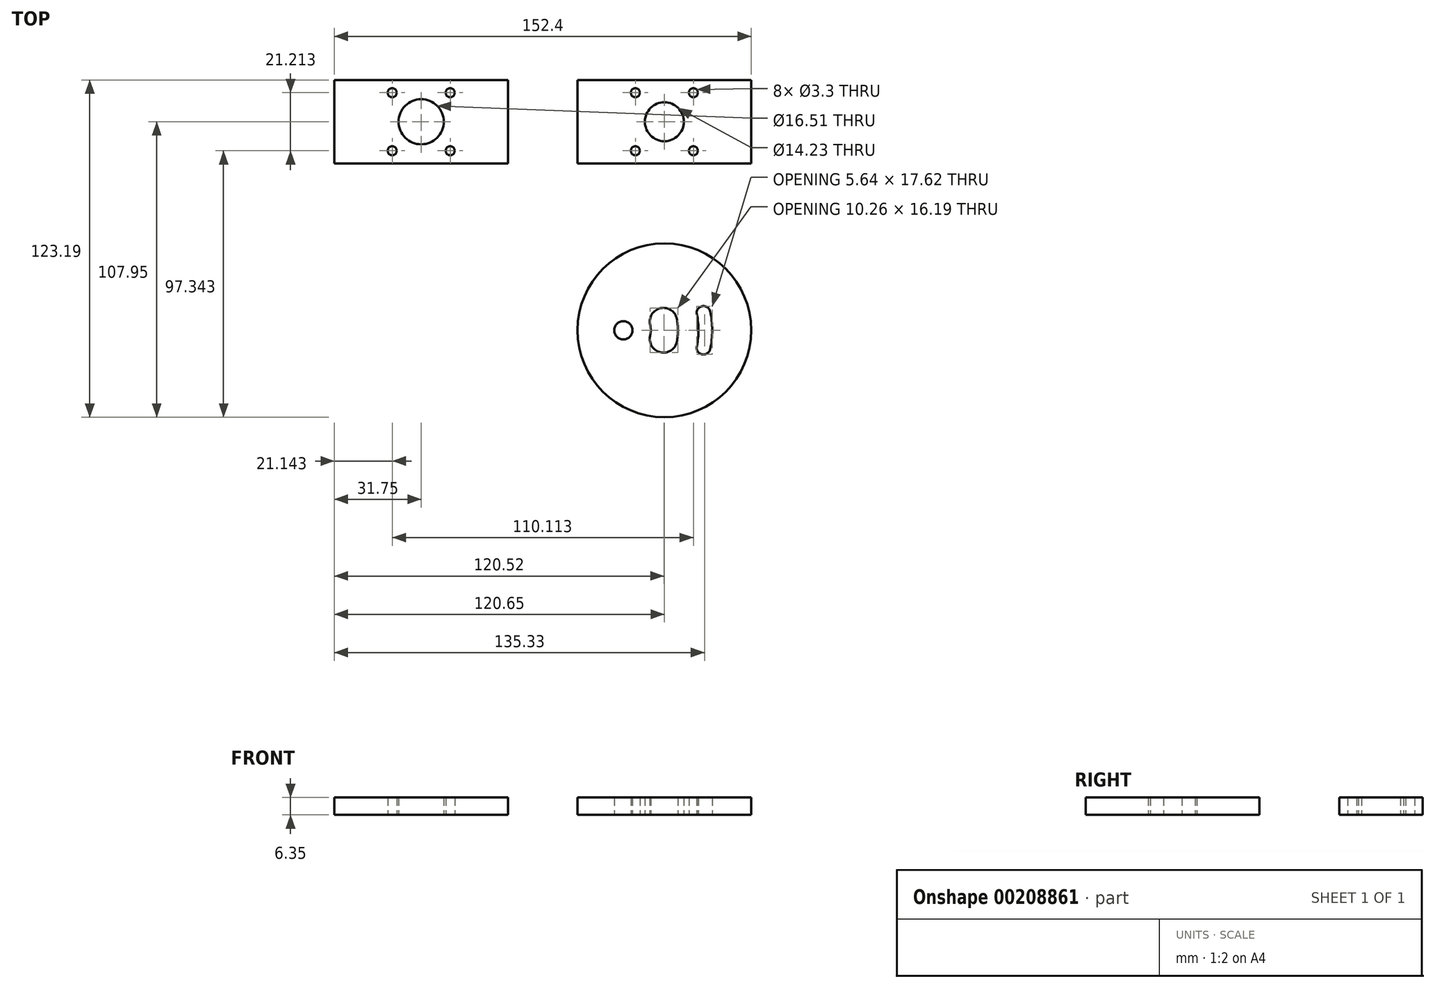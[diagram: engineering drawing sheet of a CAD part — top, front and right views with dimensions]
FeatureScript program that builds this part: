
annotation { "Feature Type Name" : "Feature", "Feature Type Description" : "" }
export const myFeature = defineFeature(function(context is Context, id is Id, definition is map)
    precondition{}
    {
        {
            var Q0;
            Q0=qCreatedBy(makeId("Top.planeOp"),FACE);
            var sketch = newSketch(context, id + "F0", { "sketchPlane" : qUnion([Q0])});
            skCircle(sketch, "E0", {"center": v(0, 0) * mm, "radius": 8.26 * mm});
            skCircle(sketch, "E1", {"center": v(88.9, 0) * mm, "radius": 7.12 * mm});
            skCircle(sketch, "E2", {"center": v(88.9, -76.2) * mm, "radius": 31.75 * mm});
            skCircle(sketch, "E3", {"center": v(73.9, -76.2) * mm, "radius": 3.35 * mm});
            skCircle(sketch, "E4", {"center": v(73.9, -76.2) * mm, "radius": 30 * mm, "construction": true});
            skArc(sketch, "E5", {"start": v(100.78, -82.02) * mm, "mid": v(101.4, -76.2) * mm, "end": v(100.78, -70.38) * mm});
            skArc(sketch, "E6", {"start": v(105.66, -83.08) * mm, "mid": v(106.4, -76.2) * mm, "end": v(105.66, -69.32) * mm});
            skCircle(sketch, "E7", {"center": v(88.9, -76.2) * mm, "radius": 15 * mm, "construction": true});
            skArc(sketch, "E8", {"start": v(103.4, -72.34) * mm, "mid": v(103.52, -72.33) * mm, "end": v(103.65, -72.31) * mm});
            skArc(sketch, "E9", {"start": v(100.78, -82.02) * mm, "mid": v(102.7, -85) * mm, "end": v(105.66, -83.08) * mm});
            skArc(sketch, "E10.trimOffspring", {"start": v(105.66, -69.32) * mm, "mid": v(102.7, -67.4) * mm, "end": v(100.78, -70.38) * mm});
            skArc(sketch, "E11.trimOffspring", {"start": v(103.65, -80.09) * mm, "mid": v(103.52, -80.07) * mm, "end": v(103.4, -80.06) * mm});
            skCircle(sketch, "E12", {"center": v(73.9, -76.2) * mm, "radius": 15 * mm, "construction": true});
            skArc(sketch, "E13", {"start": v(93.45, -71.97) * mm, "mid": v(87.5, -68.14) * mm, "end": v(83.67, -74.08) * mm});
            skArc(sketch, "E14", {"start": v(83.67, -78.32) * mm, "mid": v(87.5, -84.26) * mm, "end": v(93.45, -80.43) * mm});
            skArc(sketch, "E15.trimOffspring", {"start": v(83.67, -78.32) * mm, "mid": v(83.9, -76.2) * mm, "end": v(83.67, -74.08) * mm});
            skArc(sketch, "E16.trimOffspring", {"start": v(93.45, -80.43) * mm, "mid": v(93.9, -76.2) * mm, "end": v(93.45, -71.97) * mm});
            skLineSegment(sketch, "E17", {"start": v(-31.75, 15.24) * mm, "end": v(31.75, 15.24) * mm});
            skLineSegment(sketch, "E18.trimOffspring", {"start": v(57.15, 15.24) * mm, "end": v(120.65, 15.24) * mm});
            skLineSegment(sketch, "E19", {"start": v(0, 0) * mm, "end": v(88.9, 0) * mm, "construction": true});
            skLineSegment(sketch, "E20.0.MirrorCS", {"start": v(-31.75, -15.24) * mm, "end": v(31.75, -15.24) * mm});
            skLineSegment(sketch, "E21.0.MirrorCS", {"start": v(57.15, -15.24) * mm, "end": v(120.65, -15.24) * mm});
            skCircle(sketch, "E22", {"center": v(88.9, 0) * mm, "radius": 15 * mm, "construction": true});
            skLineSegment(sketch, "E23", {"start": v(88.9, 0) * mm, "end": v(88.9, 11.57) * mm, "construction": true});
            skLineSegment(sketch, "E24", {"start": v(88.9, 0) * mm, "end": v(76.23, 12.67) * mm, "construction": true});
            skCircle(sketch, "E25", {"center": v(78.3, 10.6) * mm, "radius": 1.65 * mm});
            skCircle(sketch, "E26.0.MirrorC", {"center": v(99.5, 10.6) * mm, "radius": 1.65 * mm});
            skCircle(sketch, "E27.0.MirrorC", {"center": v(78.3, -10.6) * mm, "radius": 1.65 * mm});
            skCircle(sketch, "E28.0.MirrorC", {"center": v(99.5, -10.6) * mm, "radius": 1.65 * mm});
            skLineSegment(sketch, "E29", {"start": v(31.75, -15.24) * mm, "end": v(31.75, 15.24) * mm});
            skLineSegment(sketch, "E30", {"start": v(-31.75, -15.24) * mm, "end": v(-31.75, 15.24) * mm});
            skLineSegment(sketch, "E31", {"start": v(57.15, 15.24) * mm, "end": v(57.15, -15.24) * mm});
            skLineSegment(sketch, "E32", {"start": v(120.65, -15.24) * mm, "end": v(120.65, 15.24) * mm});
            skPoint(sketch, "E33.center.orphan", {"position": v(15, 0) * mm});
            skPoint(sketch, "E34.center.orphan", {"position": v(0, -15) * mm});
            skPoint(sketch, "E35.center.orphan", {"position": v(-15, 0) * mm});
            skPoint(sketch, "E36.center.orphan", {"position": v(0, 15) * mm});
            skCircle(sketch, "E37", {"center": v(0, 0) * mm, "radius": 15 * mm, "construction": true});
            skCircle(sketch, "E38", {"center": v(-10.6, 10.6) * mm, "radius": 1.65 * mm});
            skLineSegment(sketch, "E39", {"start": v(0, 0) * mm, "end": v(-15.24, 15.24) * mm, "construction": true});
            skCircle(sketch, "E40.0.MirrorC", {"center": v(-10.6, -10.6) * mm, "radius": 1.65 * mm});
            skLineSegment(sketch, "E41", {"start": v(0, 0) * mm, "end": v(0, 10.83) * mm, "construction": true});
            skCircle(sketch, "E42.0.MirrorC", {"center": v(10.6, 10.6) * mm, "radius": 1.65 * mm});
            skCircle(sketch, "E43.0.MirrorC", {"center": v(10.6, -10.6) * mm, "radius": 1.65 * mm});
            skSolve(sketch);
        }
        {
            var Q0;
            Q0=qSketchRegion(id+"F0",true);
            extrude(context, id + "F1", {"entities" : qUnion([Q0]), "depth" : 6.35 * mm});
        }
    });
